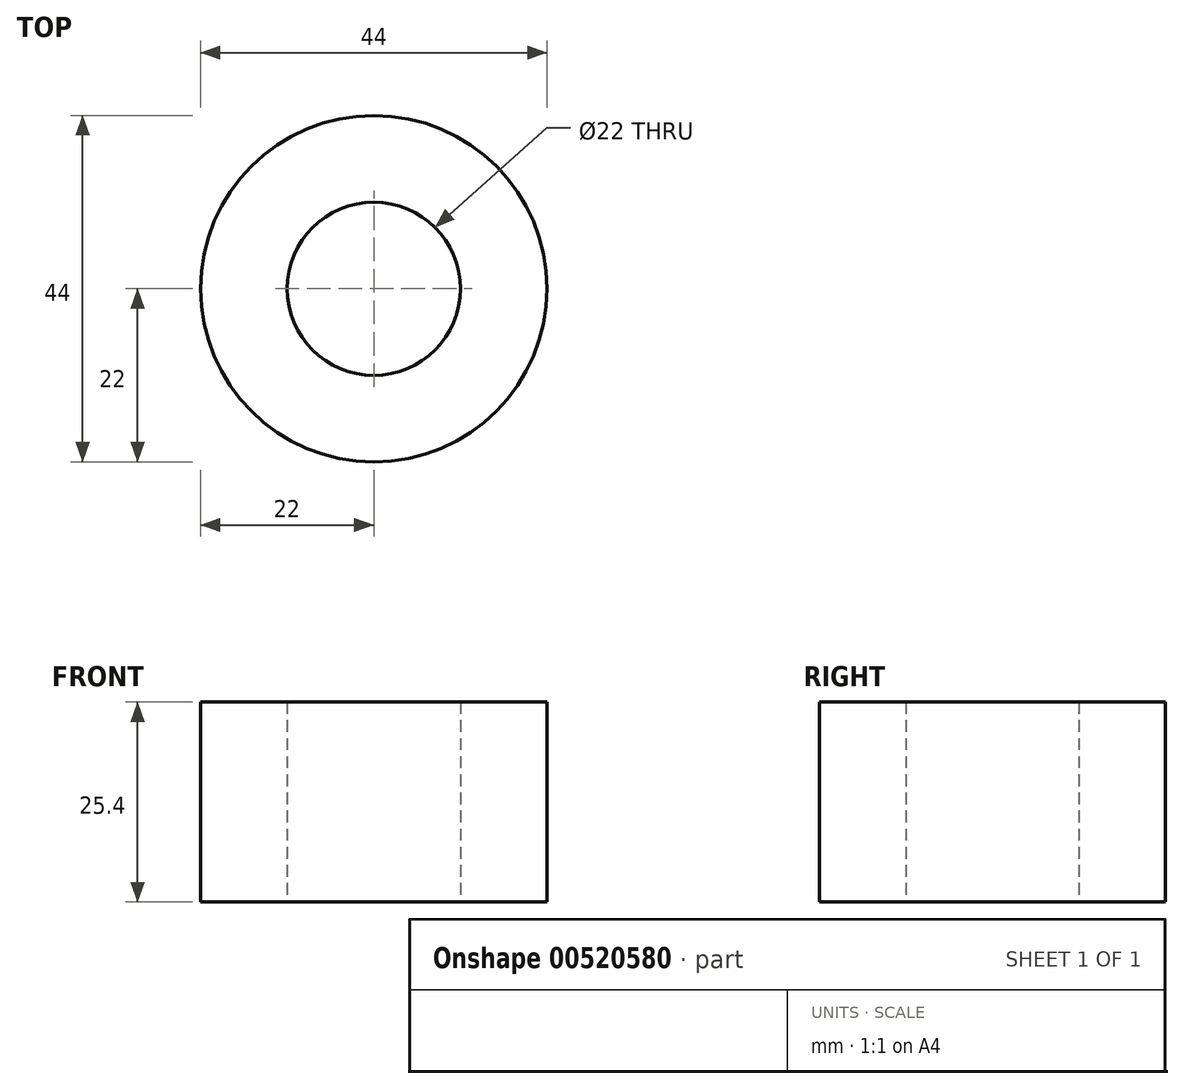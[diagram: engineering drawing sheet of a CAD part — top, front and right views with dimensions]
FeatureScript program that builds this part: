
annotation { "Feature Type Name" : "Feature", "Feature Type Description" : "" }
export const myFeature = defineFeature(function(context is Context, id is Id, definition is map)
    precondition{}
    {
        {
            var Q0;
            Q0=qCreatedBy(makeId("Top.planeOp"),FACE);
            var sketch = newSketch(context, id + "F0", { "sketchPlane" : qUnion([Q0])});
            skCircle(sketch, "E0", {"center": v(0, 0) * mm, "radius": 11 * mm});
            skCircle(sketch, "E1", {"center": v(0, 0) * mm, "radius": 22 * mm});
            skLineSegment(sketch, "E2.bottom", {"start": v(22.13, 22) * mm, "end": v(-22.13, 22) * mm});
            skLineSegment(sketch, "E2.top", {"start": v(22.13, -22) * mm, "end": v(-22.13, -22) * mm});
            skLineSegment(sketch, "E2.left", {"start": v(22.13, 22) * mm, "end": v(22.13, -22) * mm});
            skLineSegment(sketch, "E2.right", {"start": v(-22.13, 22) * mm, "end": v(-22.13, -22) * mm});
            skSolve(sketch);
        }
        {
            var Q0;
            Q0=makeQuery(id+"F0.imprint","IMPRINT",FACE,{"disambiguationData":[TD([[makeQuery(id+"F0.imprint","IMPRINT",EDGE,{"derivedFrom":sQuery(id+"F0.wireOp",EDGE,"E0")}),-1.0]])]});
            extrude(context, id + "F1", {"entities" : qUnion([Q0]), "depth" : 25.4 * mm, "offsetDistance" : 25.4 * mm});
        }
    });
